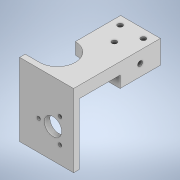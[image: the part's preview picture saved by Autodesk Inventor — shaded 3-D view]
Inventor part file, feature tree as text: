
AUTODESK INVENTOR PART (.ipt)
format: ipt  version: 2021 (Build 250183000, 183)  size: 197,120 bytes
history: native  units: in
note: dims shown in document units (in); Inventor stores cm internally (conversion verified against a paired STEP export)
features: other x3, sketch x2, extrude x1, plane x1, projected_geometry x1
ambient origin geometry x8: Origin, YZ Plane, XZ Plane, XY Plane, X Axis, Y Axis, Z Axis, Center Point
bodies: Solid1 (feature_tree)
feature tree (8):
  other  "motor_connector_left.ipt"
  extrude  "Extrusion1"  Depth=0.3937in
  other  "Solid1::motor_connector_left.ipt"
  other  "TaggingFeature1"
  sketch  "Sketch4"  dims[d0=0.3937in d1=0.5118in]
  plane  "Work Plane1"
  sketch  "Sketch17"  dims[d2=0.5118in d3=0.5118in d4=0.3937in d5=0.0in]
  projected_geometry  "Projected Loop1"
